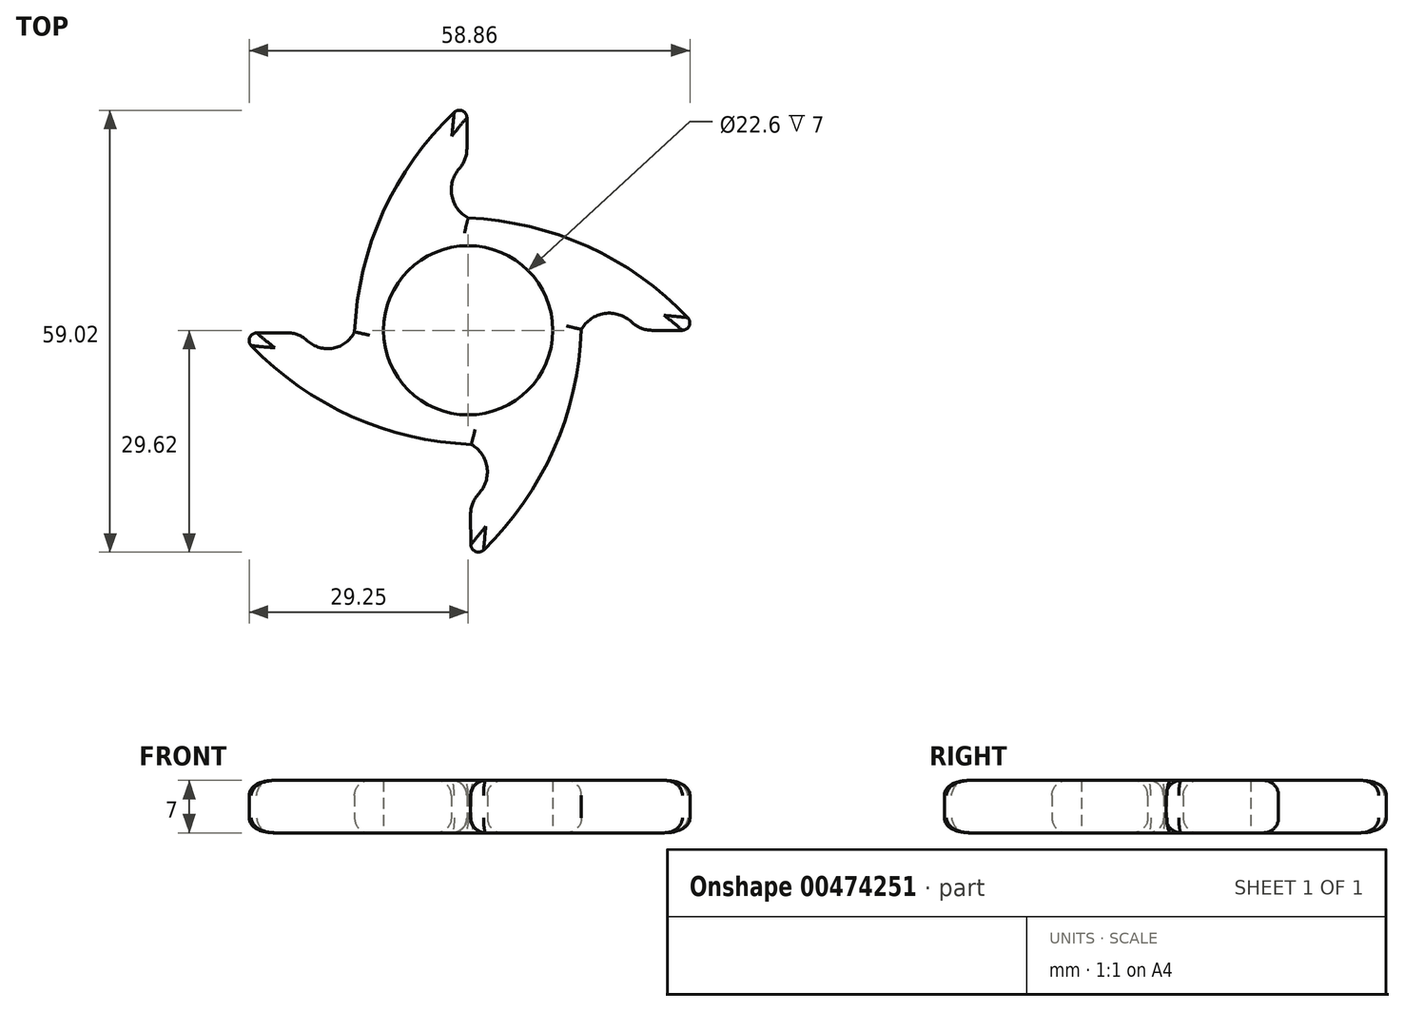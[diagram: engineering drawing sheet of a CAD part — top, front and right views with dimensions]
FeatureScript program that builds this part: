
annotation { "Feature Type Name" : "Feature", "Feature Type Description" : "" }
export const myFeature = defineFeature(function(context is Context, id is Id, definition is map)
    precondition{}
    {
        {
            var Q0;
            Q0=qCreatedBy(makeId("Top.planeOp"),FACE);
            var sketch = newSketch(context, id + "F0", { "sketchPlane" : qUnion([Q0])});
            skCircle(sketch, "E0", {"center": v(0, 0) * mm, "radius": 11.3 * mm});
            skCircle(sketch, "E1", {"center": v(0, 0) * mm, "radius": 15 * mm});
            skArc(sketch, "E2", {"start": v(30.86, 0) * mm, "mid": v(16.99, 10.7) * mm, "end": v(0, 15) * mm});
            skLineSegment(sketch, "E3", {"start": v(30.86, 0) * mm, "end": v(22.63, 0) * mm});
            skArc(sketch, "E4", {"start": v(22.63, 0) * mm, "mid": v(18.72, 3.78) * mm, "end": v(13.75, 6) * mm});
            skArc(sketch, "E5", {"start": v(0.37, -30.88) * mm, "mid": v(10.97, -16.93) * mm, "end": v(15.12, 0.1) * mm});
            skLineSegment(sketch, "E6", {"start": v(0.37, -30.88) * mm, "end": v(0.3, -22.66) * mm});
            skArc(sketch, "E7", {"start": v(0.3, -22.66) * mm, "mid": v(4.06, -18.71) * mm, "end": v(6.24, -13.72) * mm});
            skArc(sketch, "E8", {"start": v(-30.5, -0.36) * mm, "mid": v(-16.6, -11.01) * mm, "end": v(0.41, -15.24) * mm});
            skLineSegment(sketch, "E9", {"start": v(-30.5, -0.36) * mm, "end": v(-22.28, -0.33) * mm});
            skArc(sketch, "E10", {"start": v(-22.28, -0.33) * mm, "mid": v(-18.35, -4.1) * mm, "end": v(-13.37, -6.3) * mm});
            skArc(sketch, "E11", {"start": v(-0.17, 30.65) * mm, "mid": v(-10.88, 16.79) * mm, "end": v(-15.17, -0.2) * mm});
            skLineSegment(sketch, "E12", {"start": v(-0.17, 30.65) * mm, "end": v(-0.17, 22.43) * mm});
            skArc(sketch, "E13", {"start": v(-0.17, 22.43) * mm, "mid": v(-3.96, 18.51) * mm, "end": v(-6.17, 13.54) * mm});
            skArc(sketch, "E14", {"start": v(22.63, 0) * mm, "mid": v(18.9, 2.3) * mm, "end": v(15.12, 0.1) * mm});
            skArc(sketch, "E15", {"start": v(-0.17, 22.43) * mm, "mid": v(-2.26, 18.66) * mm, "end": v(0, 15) * mm});
            skArc(sketch, "E16", {"start": v(-22.28, -0.33) * mm, "mid": v(-18.69, -2.45) * mm, "end": v(-15.17, -0.2) * mm});
            skArc(sketch, "E17", {"start": v(0.3, -22.66) * mm, "mid": v(2.57, -18.98) * mm, "end": v(0.41, -15.24) * mm});
            skSolve(sketch);
        }
        {
            var Q0;
            Q0=makeQuery(id+"F0.imprint","IMPRINT",FACE,{"disambiguationData":[TD([[makeQuery(id+"F0.imprint","IMPRINT",EDGE,{"derivedFrom":sQuery(id+"F0.wireOp",EDGE,"E0")}),-1.0]])]});
            var Q1;
            {var subQ15=sQuery(id+"F0.wireOp",EDGE,"E5");Q1=makeQuery(id+"F0.imprint","IMPRINT",FACE,{"disambiguationData":[TD([[makeQuery(id+"F0.imprint","IMPRINT",EDGE,{"derivedFrom":subQ15}),1.0]])]});}
            var Q2;
            {var subQ5=sQuery(id+"F0.wireOp",EDGE,"E3");Q2=makeQuery(id+"F0.imprint","IMPRINT",FACE,{"disambiguationData":[TD([[makeQuery(id+"F0.imprint","IMPRINT",EDGE,{"derivedFrom":subQ5}),-1.0]])]});}
            var Q3;
            {var subQ0=sQuery(id+"F0.wireOp",EDGE,"E11");Q3=makeQuery(id+"F0.imprint","IMPRINT",FACE,{"disambiguationData":[TD([[makeQuery(id+"F0.imprint","IMPRINT",EDGE,{"derivedFrom":subQ0}),1.0]])]});}
            var Q4;
            {var subQ1=sQuery(id+"F0.wireOp",EDGE,"E1");var subQ3=sQuery(id+"F0.wireOp",EDGE,"E13");var subQ4=makeQuery(id+"F0.imprint","INTERSECT",VERTEX,{"derivedFrom":[subQ1,subQ3]});Q4=makeQuery(id+"F0.imprint","IMPRINT",FACE,{"disambiguationData":[TD([[makeQuery(id+"F0.imprint","IMPRINT",EDGE,{"disambiguationData":[TD([[subQ4,1.0]])],"derivedFrom":subQ3}),1.0]])]});}
            extrude(context, id + "F1", {"entities" : qUnion([Q0, Q1, Q2, Q3, Q4]), "depth" : 7 * mm});
        }
        {
            var Q0;
            Q0=makeQuery(id+"F1.opExtrude","CAP_EDGE",EDGE,{"disambiguationData":[OSD([sQuery(id+"F0.wireOp",EDGE,"E2")])],"isStart":false});
            var Q1;
            Q1=makeQuery(id+"F1.opExtrude","CAP_EDGE",EDGE,{"disambiguationData":[OSD([sQuery(id+"F0.wireOp",EDGE,"E3")])],"isStart":false});
            var Q2;
            Q2=makeQuery(id+"F1.opExtrude","CAP_EDGE",EDGE,{"disambiguationData":[OSD([sQuery(id+"F0.wireOp",EDGE,"E14")])],"isStart":false});
            var Q3;
            Q3=makeQuery(id+"F1.opExtrude","CAP_EDGE",EDGE,{"disambiguationData":[OSD([sQuery(id+"F0.wireOp",EDGE,"E5")])],"isStart":false});
            var Q4;
            Q4=makeQuery(id+"F1.opExtrude","CAP_EDGE",EDGE,{"disambiguationData":[OSD([sQuery(id+"F0.wireOp",EDGE,"E6")])],"isStart":false});
            var Q5;
            Q5=makeQuery(id+"F1.opExtrude","CAP_EDGE",EDGE,{"disambiguationData":[OSD([sQuery(id+"F0.wireOp",EDGE,"E17")])],"isStart":false});
            var Q6;
            Q6=makeQuery(id+"F1.opExtrude","CAP_EDGE",EDGE,{"disambiguationData":[OSD([sQuery(id+"F0.wireOp",EDGE,"E8")])],"isStart":false});
            var Q7;
            Q7=makeQuery(id+"F1.opExtrude","CAP_EDGE",EDGE,{"disambiguationData":[OSD([sQuery(id+"F0.wireOp",EDGE,"E16")])],"isStart":false});
            var Q8;
            Q8=makeQuery(id+"F1.opExtrude","CAP_EDGE",EDGE,{"disambiguationData":[OSD([sQuery(id+"F0.wireOp",EDGE,"E9")])],"isStart":false});
            var Q9;
            Q9=makeQuery(id+"F1.opExtrude","CAP_EDGE",EDGE,{"disambiguationData":[OSD([sQuery(id+"F0.wireOp",EDGE,"E11")])],"isStart":false});
            var Q10;
            Q10=makeQuery(id+"F1.opExtrude","CAP_EDGE",EDGE,{"disambiguationData":[OSD([sQuery(id+"F0.wireOp",EDGE,"E12")])],"isStart":false});
            var Q11;
            Q11=makeQuery(id+"F1.opExtrude","CAP_EDGE",EDGE,{"disambiguationData":[OSD([sQuery(id+"F0.wireOp",EDGE,"E15")])],"isStart":false});
            fillet(context, id + "F2", {"entities" : qUnion([Q0, Q1, Q2, Q3, Q4, Q5, Q6, Q7, Q8, Q9, Q10, Q11]), "radius" : 2 * mm, "tangentPropagation" : true, "allowEdgeOverflow" : false});
        }
        {
            var Q0;
            Q0=makeQuery(id+"F1.opExtrude","CAP_EDGE",EDGE,{"disambiguationData":[OSD([sQuery(id+"F0.wireOp",EDGE,"E5")])],"isStart":true});
            var Q1;
            Q1=makeQuery(id+"F1.opExtrude","CAP_EDGE",EDGE,{"disambiguationData":[OSD([sQuery(id+"F0.wireOp",EDGE,"E14")])],"isStart":true});
            var Q2;
            Q2=makeQuery(id+"F1.opExtrude","CAP_EDGE",EDGE,{"disambiguationData":[OSD([sQuery(id+"F0.wireOp",EDGE,"E3")])],"isStart":true});
            var Q3;
            Q3=makeQuery(id+"F1.opExtrude","CAP_EDGE",EDGE,{"disambiguationData":[OSD([sQuery(id+"F0.wireOp",EDGE,"E2")])],"isStart":true});
            var Q4;
            Q4=makeQuery(id+"F1.opExtrude","CAP_EDGE",EDGE,{"disambiguationData":[OSD([sQuery(id+"F0.wireOp",EDGE,"E15")])],"isStart":true});
            var Q5;
            Q5=makeQuery(id+"F1.opExtrude","CAP_EDGE",EDGE,{"disambiguationData":[OSD([sQuery(id+"F0.wireOp",EDGE,"E12")])],"isStart":true});
            var Q6;
            Q6=makeQuery(id+"F1.opExtrude","CAP_EDGE",EDGE,{"disambiguationData":[OSD([sQuery(id+"F0.wireOp",EDGE,"E11")])],"isStart":true});
            var Q7;
            Q7=makeQuery(id+"F1.opExtrude","CAP_EDGE",EDGE,{"disambiguationData":[OSD([sQuery(id+"F0.wireOp",EDGE,"E16")])],"isStart":true});
            var Q8;
            Q8=makeQuery(id+"F1.opExtrude","CAP_EDGE",EDGE,{"disambiguationData":[OSD([sQuery(id+"F0.wireOp",EDGE,"E9")])],"isStart":true});
            var Q9;
            Q9=makeQuery(id+"F1.opExtrude","CAP_EDGE",EDGE,{"disambiguationData":[OSD([sQuery(id+"F0.wireOp",EDGE,"E8")])],"isStart":true});
            var Q10;
            Q10=makeQuery(id+"F1.opExtrude","CAP_EDGE",EDGE,{"disambiguationData":[OSD([sQuery(id+"F0.wireOp",EDGE,"E17")])],"isStart":true});
            var Q11;
            Q11=makeQuery(id+"F1.opExtrude","CAP_EDGE",EDGE,{"disambiguationData":[OSD([sQuery(id+"F0.wireOp",EDGE,"E6")])],"isStart":true});
            fillet(context, id + "F3", {"entities" : qUnion([Q0, Q1, Q2, Q3, Q4, Q5, Q6, Q7, Q8, Q9, Q10, Q11]), "radius" : 2 * mm, "tangentPropagation" : true, "allowEdgeOverflow" : false});
        }
        {
            var Q0;
            Q0=makeQuery(id+"F1.opExtrude","SWEPT_EDGE",EDGE,{"disambiguationData":[OSD([sQuery(id+"F0.wireOp",EDGE,"E5"),sQuery(id+"F0.wireOp",EDGE,"E6")])]});
            var Q1;
            Q1=makeQuery(id+"F2.opFillet","BLEND_EDGE",EDGE,{"blendedFrom":[makeQuery(id+"F1.opExtrude","CAP_EDGE",EDGE,{"disambiguationData":[OSD([sQuery(id+"F0.wireOp",EDGE,"E5")])],"isStart":false}),makeQuery(id+"F1.opExtrude","CAP_EDGE",EDGE,{"disambiguationData":[OSD([sQuery(id+"F0.wireOp",EDGE,"E6")])],"isStart":false})],"blendedInto":[]});
            var Q2;
            Q2=makeQuery(id+"F3.opFillet","BLEND_EDGE",EDGE,{"blendedFrom":[makeQuery(id+"F1.opExtrude","CAP_EDGE",EDGE,{"disambiguationData":[OSD([sQuery(id+"F0.wireOp",EDGE,"E5")])],"isStart":true}),makeQuery(id+"F1.opExtrude","CAP_EDGE",EDGE,{"disambiguationData":[OSD([sQuery(id+"F0.wireOp",EDGE,"E6")])],"isStart":true})],"blendedInto":[]});
            var Q3;
            Q3=makeQuery(id+"F1.opExtrude","SWEPT_EDGE",EDGE,{"disambiguationData":[OSD([sQuery(id+"F0.wireOp",EDGE,"E2"),sQuery(id+"F0.wireOp",EDGE,"E3")])]});
            var Q4;
            Q4=makeQuery(id+"F2.opFillet","BLEND_EDGE",EDGE,{"blendedFrom":[makeQuery(id+"F1.opExtrude","CAP_EDGE",EDGE,{"disambiguationData":[OSD([sQuery(id+"F0.wireOp",EDGE,"E2")])],"isStart":false}),makeQuery(id+"F1.opExtrude","CAP_EDGE",EDGE,{"disambiguationData":[OSD([sQuery(id+"F0.wireOp",EDGE,"E3")])],"isStart":false})],"blendedInto":[]});
            var Q5;
            Q5=makeQuery(id+"F3.opFillet","BLEND_EDGE",EDGE,{"blendedFrom":[makeQuery(id+"F1.opExtrude","CAP_EDGE",EDGE,{"disambiguationData":[OSD([sQuery(id+"F0.wireOp",EDGE,"E2")])],"isStart":true}),makeQuery(id+"F1.opExtrude","CAP_EDGE",EDGE,{"disambiguationData":[OSD([sQuery(id+"F0.wireOp",EDGE,"E3")])],"isStart":true})],"blendedInto":[]});
            var Q6;
            Q6=makeQuery(id+"F2.opFillet","BLEND_EDGE",EDGE,{"blendedFrom":[makeQuery(id+"F1.opExtrude","CAP_EDGE",EDGE,{"disambiguationData":[OSD([sQuery(id+"F0.wireOp",EDGE,"E8")])],"isStart":false}),makeQuery(id+"F1.opExtrude","CAP_EDGE",EDGE,{"disambiguationData":[OSD([sQuery(id+"F0.wireOp",EDGE,"E9")])],"isStart":false})],"blendedInto":[]});
            var Q7;
            Q7=makeQuery(id+"F1.opExtrude","SWEPT_EDGE",EDGE,{"disambiguationData":[OSD([sQuery(id+"F0.wireOp",EDGE,"E8"),sQuery(id+"F0.wireOp",EDGE,"E9")])]});
            var Q8;
            Q8=makeQuery(id+"F3.opFillet","BLEND_EDGE",EDGE,{"blendedFrom":[makeQuery(id+"F1.opExtrude","CAP_EDGE",EDGE,{"disambiguationData":[OSD([sQuery(id+"F0.wireOp",EDGE,"E8")])],"isStart":true}),makeQuery(id+"F1.opExtrude","CAP_EDGE",EDGE,{"disambiguationData":[OSD([sQuery(id+"F0.wireOp",EDGE,"E9")])],"isStart":true})],"blendedInto":[]});
            var Q9;
            Q9=makeQuery(id+"F2.opFillet","BLEND_EDGE",EDGE,{"blendedFrom":[makeQuery(id+"F1.opExtrude","CAP_EDGE",EDGE,{"disambiguationData":[OSD([sQuery(id+"F0.wireOp",EDGE,"E11")])],"isStart":false}),makeQuery(id+"F1.opExtrude","CAP_EDGE",EDGE,{"disambiguationData":[OSD([sQuery(id+"F0.wireOp",EDGE,"E12")])],"isStart":false})],"blendedInto":[]});
            var Q10;
            Q10=makeQuery(id+"F1.opExtrude","SWEPT_EDGE",EDGE,{"disambiguationData":[OSD([sQuery(id+"F0.wireOp",EDGE,"E11"),sQuery(id+"F0.wireOp",EDGE,"E12")])]});
            var Q11;
            Q11=makeQuery(id+"F3.opFillet","BLEND_EDGE",EDGE,{"blendedFrom":[makeQuery(id+"F1.opExtrude","CAP_EDGE",EDGE,{"disambiguationData":[OSD([sQuery(id+"F0.wireOp",EDGE,"E11")])],"isStart":true}),makeQuery(id+"F1.opExtrude","CAP_EDGE",EDGE,{"disambiguationData":[OSD([sQuery(id+"F0.wireOp",EDGE,"E12")])],"isStart":true})],"blendedInto":[]});
            fillet(context, id + "F4", {"entities" : qUnion([Q0, Q1, Q2, Q3, Q4, Q5, Q6, Q7, Q8, Q9, Q10, Q11]), "radius" : 1 * mm, "tangentPropagation" : true, "allowEdgeOverflow" : false});
        }
        {
            var Q0;
            Q0=makeQuery(id+"F1.opExtrude","SWEPT_EDGE",EDGE,{"disambiguationData":[OSD([sQuery(id+"F0.wireOp",EDGE,"E9"),sQuery(id+"F0.wireOp",EDGE,"E10"),sQuery(id+"F0.wireOp",EDGE,"E16")])]});
            var Q1;
            Q1=makeQuery(id+"F2.opFillet","BLEND_EDGE",EDGE,{"blendedFrom":[makeQuery(id+"F1.opExtrude","CAP_EDGE",EDGE,{"disambiguationData":[OSD([sQuery(id+"F0.wireOp",EDGE,"E9")])],"isStart":false}),makeQuery(id+"F1.opExtrude","CAP_EDGE",EDGE,{"disambiguationData":[OSD([sQuery(id+"F0.wireOp",EDGE,"E16")])],"isStart":false})],"blendedInto":[]});
            var Q2;
            Q2=makeQuery(id+"F3.opFillet","BLEND_EDGE",EDGE,{"blendedFrom":[makeQuery(id+"F1.opExtrude","CAP_EDGE",EDGE,{"disambiguationData":[OSD([sQuery(id+"F0.wireOp",EDGE,"E9")])],"isStart":true}),makeQuery(id+"F1.opExtrude","CAP_EDGE",EDGE,{"disambiguationData":[OSD([sQuery(id+"F0.wireOp",EDGE,"E16")])],"isStart":true})],"blendedInto":[]});
            var Q3;
            Q3=makeQuery(id+"F1.opExtrude","SWEPT_EDGE",EDGE,{"disambiguationData":[OSD([sQuery(id+"F0.wireOp",EDGE,"E12"),sQuery(id+"F0.wireOp",EDGE,"E13"),sQuery(id+"F0.wireOp",EDGE,"E15")])]});
            var Q4;
            Q4=makeQuery(id+"F3.opFillet","BLEND_EDGE",EDGE,{"blendedFrom":[makeQuery(id+"F1.opExtrude","CAP_EDGE",EDGE,{"disambiguationData":[OSD([sQuery(id+"F0.wireOp",EDGE,"E12")])],"isStart":true}),makeQuery(id+"F1.opExtrude","CAP_EDGE",EDGE,{"disambiguationData":[OSD([sQuery(id+"F0.wireOp",EDGE,"E15")])],"isStart":true})],"blendedInto":[]});
            var Q5;
            Q5=makeQuery(id+"F2.opFillet","BLEND_EDGE",EDGE,{"blendedFrom":[makeQuery(id+"F1.opExtrude","CAP_EDGE",EDGE,{"disambiguationData":[OSD([sQuery(id+"F0.wireOp",EDGE,"E12")])],"isStart":false}),makeQuery(id+"F1.opExtrude","CAP_EDGE",EDGE,{"disambiguationData":[OSD([sQuery(id+"F0.wireOp",EDGE,"E15")])],"isStart":false})],"blendedInto":[]});
            var Q6;
            Q6=makeQuery(id+"F3.opFillet","BLEND_EDGE",EDGE,{"blendedFrom":[makeQuery(id+"F1.opExtrude","CAP_EDGE",EDGE,{"disambiguationData":[OSD([sQuery(id+"F0.wireOp",EDGE,"E3")])],"isStart":true}),makeQuery(id+"F1.opExtrude","CAP_EDGE",EDGE,{"disambiguationData":[OSD([sQuery(id+"F0.wireOp",EDGE,"E14")])],"isStart":true})],"blendedInto":[]});
            var Q7;
            Q7=makeQuery(id+"F1.opExtrude","SWEPT_EDGE",EDGE,{"disambiguationData":[OSD([sQuery(id+"F0.wireOp",EDGE,"E3"),sQuery(id+"F0.wireOp",EDGE,"E4"),sQuery(id+"F0.wireOp",EDGE,"E14")])]});
            var Q8;
            Q8=makeQuery(id+"F2.opFillet","BLEND_EDGE",EDGE,{"blendedFrom":[makeQuery(id+"F1.opExtrude","CAP_EDGE",EDGE,{"disambiguationData":[OSD([sQuery(id+"F0.wireOp",EDGE,"E3")])],"isStart":false}),makeQuery(id+"F1.opExtrude","CAP_EDGE",EDGE,{"disambiguationData":[OSD([sQuery(id+"F0.wireOp",EDGE,"E14")])],"isStart":false})],"blendedInto":[]});
            var Q9;
            Q9=makeQuery(id+"F1.opExtrude","SWEPT_EDGE",EDGE,{"disambiguationData":[OSD([sQuery(id+"F0.wireOp",EDGE,"E6"),sQuery(id+"F0.wireOp",EDGE,"E7"),sQuery(id+"F0.wireOp",EDGE,"E17")])]});
            var Q10;
            Q10=makeQuery(id+"F3.opFillet","BLEND_EDGE",EDGE,{"blendedFrom":[makeQuery(id+"F1.opExtrude","CAP_EDGE",EDGE,{"disambiguationData":[OSD([sQuery(id+"F0.wireOp",EDGE,"E6")])],"isStart":true}),makeQuery(id+"F1.opExtrude","CAP_EDGE",EDGE,{"disambiguationData":[OSD([sQuery(id+"F0.wireOp",EDGE,"E17")])],"isStart":true})],"blendedInto":[]});
            var Q11;
            Q11=makeQuery(id+"F2.opFillet","BLEND_EDGE",EDGE,{"blendedFrom":[makeQuery(id+"F1.opExtrude","CAP_EDGE",EDGE,{"disambiguationData":[OSD([sQuery(id+"F0.wireOp",EDGE,"E6")])],"isStart":false}),makeQuery(id+"F1.opExtrude","CAP_EDGE",EDGE,{"disambiguationData":[OSD([sQuery(id+"F0.wireOp",EDGE,"E17")])],"isStart":false})],"blendedInto":[]});
            fillet(context, id + "F5", {"entities" : qUnion([Q0, Q1, Q2, Q3, Q4, Q5, Q6, Q7, Q8, Q9, Q10, Q11]), "radius" : 4 * mm, "tangentPropagation" : true, "allowEdgeOverflow" : false});
        }
    });
